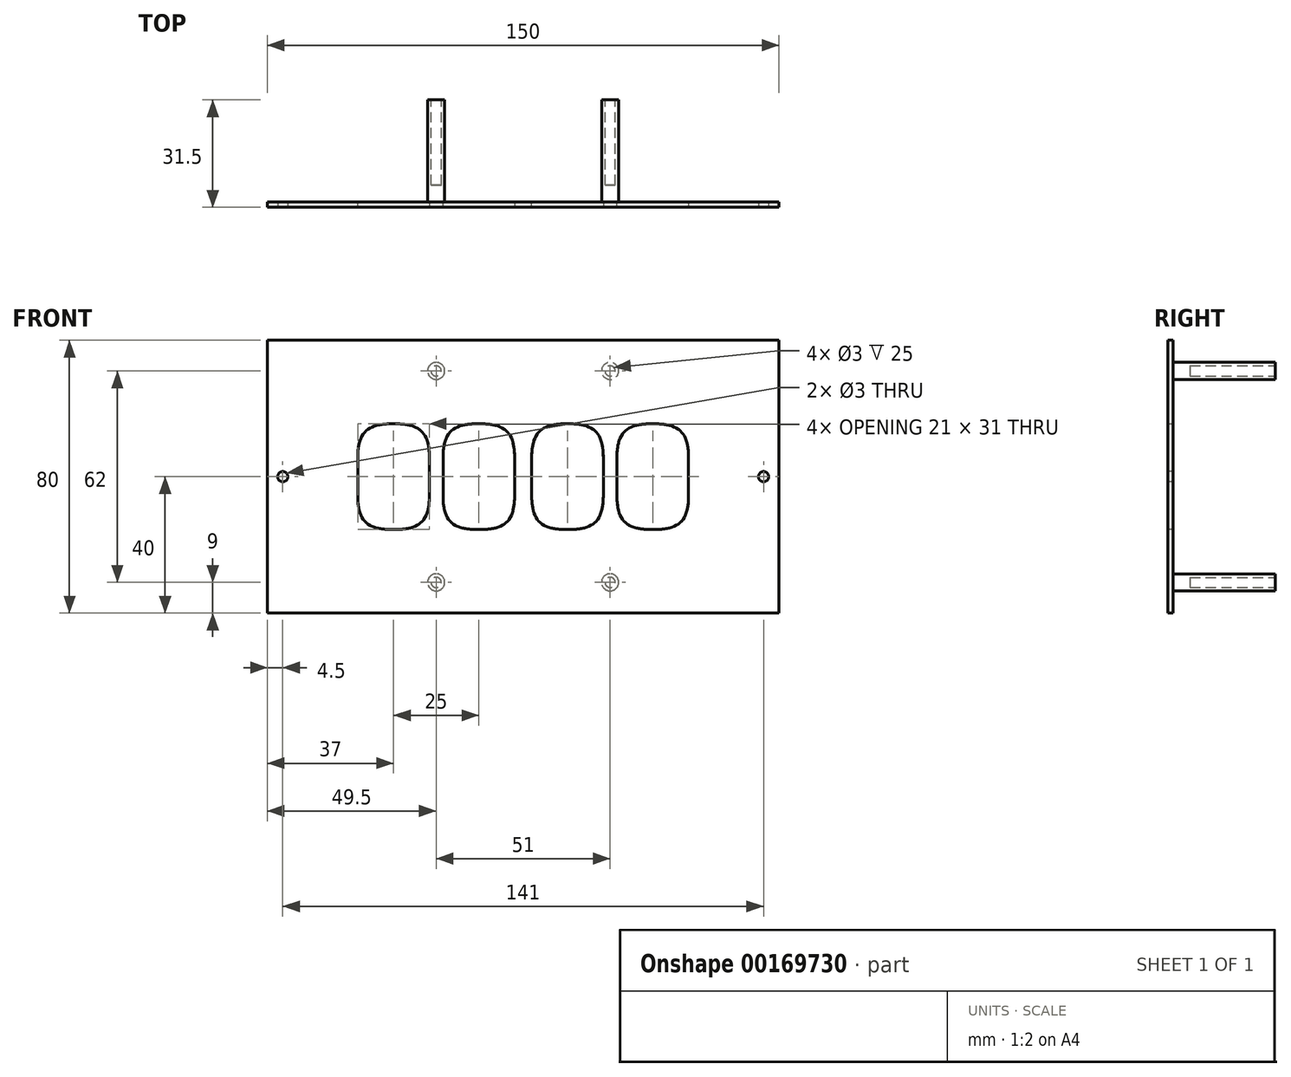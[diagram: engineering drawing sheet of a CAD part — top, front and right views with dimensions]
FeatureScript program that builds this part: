
annotation { "Feature Type Name" : "Feature", "Feature Type Description" : "" }
export const myFeature = defineFeature(function(context is Context, id is Id, definition is map)
    precondition{}
    {
        {
            var Q0;
            Q0=qCreatedBy(makeId("Front.planeOp"),FACE);
            var sketch = newSketch(context, id + "F0", { "sketchPlane" : qUnion([Q0])});
            skLineSegment(sketch, "E0.bottom", {"start": v(75, 40) * mm, "end": v(-75, 40) * mm});
            skLineSegment(sketch, "E0.top", {"start": v(75, -40) * mm, "end": v(-75, -40) * mm});
            skLineSegment(sketch, "E0.left", {"start": v(75, 40) * mm, "end": v(75, -40) * mm});
            skLineSegment(sketch, "E0.right", {"start": v(-75, 40) * mm, "end": v(-75, -40) * mm});
            skSolve(sketch);
        }
        {
            var Q0;
            Q0=makeQuery(id+"F0.imprint","IMPRINT",FACE,{"disambiguationData":[TD([[makeQuery(id+"F0.imprint","IMPRINT",EDGE,{"derivedFrom":sQuery(id+"F0.wireOp",EDGE,"E0.bottom")}),1.0]])]});
            extrude(context, id + "F1", {"entities" : qUnion([Q0]), "depth" : 1.5 * mm});
        }
        {
            var Q0;
            Q0=makeQuery(id+"F1.opExtrude","CAP_FACE",FACE,{"disambiguationData":[OSD([sQuery(id+"F0.wireOp",EDGE,"E0.bottom"),sQuery(id+"F0.wireOp",EDGE,"E0.top"),sQuery(id+"F0.wireOp",EDGE,"E0.left"),sQuery(id+"F0.wireOp",EDGE,"E0.right")])],"isStart":true});
            var sketch = newSketch(context, id + "F2", { "sketchPlane" : qUnion([Q0])});
            skCircle(sketch, "E1", {"center": v(-25.5, 31) * mm, "radius": 2.5 * mm});
            skCircle(sketch, "E2", {"center": v(-25.5, -31) * mm, "radius": 2.5 * mm});
            skCircle(sketch, "E3", {"center": v(25.5, -31) * mm, "radius": 2.5 * mm});
            skCircle(sketch, "E4", {"center": v(25.5, 31) * mm, "radius": 2.5 * mm});
            skSolve(sketch);
        }
        {
            var Q0;
            Q0 = qSketchRegion(id + "F2", true);
            extrude(context, id + "F3", {"entities" : qUnion([Q0]), "operationType" : NewBodyOperationType.ADD, "depth" : 30 * mm});
        }
        {
            var Q0;
            Q0=makeQuery(id+"F3.opExtrude","CAP_FACE",FACE,{"disambiguationData":[OSD([sQuery(id+"F2.wireOp",EDGE,"E1")])],"isStart":false});
            var sketch = newSketch(context, id + "F4", { "sketchPlane" : qUnion([Q0])});
            skCircle(sketch, "E5", {"center": v(-25.5, 31) * mm, "radius": 1.5 * mm});
            skSolve(sketch);
        }
        {
            var Q0;
            Q0=makeQuery(id+"F3.opExtrude","CAP_FACE",FACE,{"disambiguationData":[OSD([sQuery(id+"F2.wireOp",EDGE,"E4")])],"isStart":false});
            var sketch = newSketch(context, id + "F5", { "sketchPlane" : qUnion([Q0])});
            skCircle(sketch, "E6", {"center": v(25.5, 31) * mm, "radius": 1.5 * mm});
            skSolve(sketch);
        }
        {
            var Q0;
            Q0=makeQuery(id+"F3.opExtrude","CAP_FACE",FACE,{"disambiguationData":[OSD([sQuery(id+"F2.wireOp",EDGE,"E2")])],"isStart":false});
            var sketch = newSketch(context, id + "F6", { "sketchPlane" : qUnion([Q0])});
            skCircle(sketch, "E7", {"center": v(-25.5, -31) * mm, "radius": 1.5 * mm});
            skSolve(sketch);
        }
        {
            var Q0;
            Q0=makeQuery(id+"F3.opExtrude","CAP_FACE",FACE,{"disambiguationData":[OSD([sQuery(id+"F2.wireOp",EDGE,"E3")])],"isStart":false});
            var sketch = newSketch(context, id + "F7", { "sketchPlane" : qUnion([Q0])});
            skCircle(sketch, "E8", {"center": v(25.5, -31) * mm, "radius": 1.5 * mm});
            skSolve(sketch);
        }
        {
            var Q0;
            Q0 = qSketchRegion(id + "F4", true);
            var Q1;
            Q1 = qSketchRegion(id + "F5", true);
            var Q2;
            Q2 = qSketchRegion(id + "F6", true);
            var Q3;
            Q3 = qSketchRegion(id + "F7", true);
            extrude(context, id + "F8", {"entities" : qUnion([Q0, Q1, Q2, Q3]), "operationType" : NewBodyOperationType.REMOVE, "oppositeDirection" : true, "depth" : 25 * mm});
        }
        {
            var Q0;
            Q0=makeQuery(id+"F1.opExtrude","CAP_FACE",FACE,{"disambiguationData":[OSD([sQuery(id+"F0.wireOp",EDGE,"E0.bottom"),sQuery(id+"F0.wireOp",EDGE,"E0.top"),sQuery(id+"F0.wireOp",EDGE,"E0.left"),sQuery(id+"F0.wireOp",EDGE,"E0.right")])],"isStart":false});
            var sketch = newSketch(context, id + "F9", { "sketchPlane" : qUnion([Q0])});
            skCircle(sketch, "E9", {"center": v(-70.5, 0) * mm, "radius": 1.5 * mm});
            skLineSegment(sketch, "E10.bottom", {"start": v(-48.5, 15.5) * mm, "end": v(-27.5, 15.5) * mm});
            skLineSegment(sketch, "E10.top", {"start": v(-48.5, -15.5) * mm, "end": v(-27.5, -15.5) * mm});
            skLineSegment(sketch, "E10.left", {"start": v(-48.5, 15.5) * mm, "end": v(-48.5, -15.5) * mm});
            skLineSegment(sketch, "E10.right", {"start": v(-27.5, 15.5) * mm, "end": v(-27.5, -15.5) * mm});
            skLineSegment(sketch, "E11.bottom", {"start": v(-23.5, 15.5) * mm, "end": v(-2.5, 15.5) * mm});
            skLineSegment(sketch, "E11.top", {"start": v(-23.5, -15.5) * mm, "end": v(-2.5, -15.5) * mm});
            skLineSegment(sketch, "E11.left", {"start": v(-23.5, 15.5) * mm, "end": v(-23.5, -15.5) * mm});
            skLineSegment(sketch, "E11.right", {"start": v(-2.5, 15.5) * mm, "end": v(-2.5, -15.5) * mm});
            skSolve(sketch);
        }
        {
            var Q0;
            Q0 = qSketchRegion(id + "F9", true);
            extrude(context, id + "F10", {"entities" : qUnion([Q0]), "operationType" : NewBodyOperationType.REMOVE, "oppositeDirection" : true, "depth" : 3 * mm});
        }
        {
            var Q0;
            Q0=makeQuery(id+"F10.boolean.opBoolean","COPY",FACE,{"derivedFrom":makeQuery(id+"F10.opExtrude","SWEPT_FACE",FACE,{"disambiguationData":[OSD([sQuery(id+"F9.wireOp",EDGE,"E9")])]})});
            var Q1;
            Q1=makeQuery(id+"F10.boolean.opBoolean","COPY",FACE,{"derivedFrom":makeQuery(id+"F10.opExtrude","SWEPT_FACE",FACE,{"disambiguationData":[OSD([sQuery(id+"F9.wireOp",EDGE,"E10.left")])]})});
            var Q2;
            Q2=makeQuery(id+"F10.boolean.opBoolean","COPY",FACE,{"derivedFrom":makeQuery(id+"F10.opExtrude","SWEPT_FACE",FACE,{"disambiguationData":[OSD([sQuery(id+"F9.wireOp",EDGE,"E11.left")])]})});
            var Q3;
            Q3=makeQuery(id+"F10.boolean.opBoolean","COPY",FACE,{"derivedFrom":makeQuery(id+"F10.opExtrude","SWEPT_FACE",FACE,{"disambiguationData":[OSD([sQuery(id+"F9.wireOp",EDGE,"E10.bottom")])]})});
            var Q4;
            Q4=makeQuery(id+"F10.boolean.opBoolean","COPY",FACE,{"derivedFrom":makeQuery(id+"F10.opExtrude","SWEPT_FACE",FACE,{"disambiguationData":[OSD([sQuery(id+"F9.wireOp",EDGE,"E10.right")])]})});
            var Q5;
            Q5=makeQuery(id+"F10.boolean.opBoolean","COPY",FACE,{"derivedFrom":makeQuery(id+"F10.opExtrude","SWEPT_FACE",FACE,{"disambiguationData":[OSD([sQuery(id+"F9.wireOp",EDGE,"E11.bottom")])]})});
            var Q6;
            Q6=makeQuery(id+"F10.boolean.opBoolean","COPY",FACE,{"derivedFrom":makeQuery(id+"F10.opExtrude","SWEPT_FACE",FACE,{"disambiguationData":[OSD([sQuery(id+"F9.wireOp",EDGE,"E11.right")])]})});
            var Q7;
            Q7=makeQuery(id+"F10.boolean.opBoolean","COPY",FACE,{"derivedFrom":makeQuery(id+"F10.opExtrude","SWEPT_FACE",FACE,{"disambiguationData":[OSD([sQuery(id+"F9.wireOp",EDGE,"E11.top")])]})});
            var Q8;
            Q8=makeQuery(id+"F10.boolean.opBoolean","COPY",FACE,{"derivedFrom":makeQuery(id+"F10.opExtrude","SWEPT_FACE",FACE,{"disambiguationData":[OSD([sQuery(id+"F9.wireOp",EDGE,"E10.top")])]})});
            var Q9;
            Q9=qCreatedBy(makeId("Right.planeOp"),FACE);
            mirror(context, id + "F11", {"patternType" : MirrorType.FACE, "faces" : qUnion([Q0, Q1, Q2, Q3, Q4, Q5, Q6, Q7, Q8]), "mirrorPlane" : qUnion([Q9])});
        }
        {
            var Q0;
            Q0=makeQuery(id+"F10.boolean.opBoolean","COPY",EDGE,{"derivedFrom":makeQuery(id+"F10.opExtrude","SWEPT_EDGE",EDGE,{"disambiguationData":[OSD([sQuery(id+"F9.wireOp",EDGE,"E10.bottom"),sQuery(id+"F9.wireOp",EDGE,"E10.left")])]})});
            var Q1;
            Q1=makeQuery(id+"F10.boolean.opBoolean","COPY",EDGE,{"derivedFrom":makeQuery(id+"F10.opExtrude","SWEPT_EDGE",EDGE,{"disambiguationData":[OSD([sQuery(id+"F9.wireOp",EDGE,"E10.bottom"),sQuery(id+"F9.wireOp",EDGE,"E10.right")])]})});
            var Q2;
            Q2=makeQuery(id+"F10.boolean.opBoolean","COPY",EDGE,{"derivedFrom":makeQuery(id+"F10.opExtrude","SWEPT_EDGE",EDGE,{"disambiguationData":[OSD([sQuery(id+"F9.wireOp",EDGE,"E10.top"),sQuery(id+"F9.wireOp",EDGE,"E10.left")])]})});
            var Q3;
            Q3=makeQuery(id+"F10.boolean.opBoolean","COPY",EDGE,{"derivedFrom":makeQuery(id+"F10.opExtrude","SWEPT_EDGE",EDGE,{"disambiguationData":[OSD([sQuery(id+"F9.wireOp",EDGE,"E10.top"),sQuery(id+"F9.wireOp",EDGE,"E10.right")])]})});
            var Q4;
            Q4=makeQuery(id+"F10.boolean.opBoolean","COPY",EDGE,{"derivedFrom":makeQuery(id+"F10.opExtrude","SWEPT_EDGE",EDGE,{"disambiguationData":[OSD([sQuery(id+"F9.wireOp",EDGE,"E11.top"),sQuery(id+"F9.wireOp",EDGE,"E11.right")])]})});
            var Q5;
            Q5=makeQuery(id+"F10.boolean.opBoolean","COPY",EDGE,{"derivedFrom":makeQuery(id+"F10.opExtrude","SWEPT_EDGE",EDGE,{"disambiguationData":[OSD([sQuery(id+"F9.wireOp",EDGE,"E11.bottom"),sQuery(id+"F9.wireOp",EDGE,"E11.left")])]})});
            var Q6;
            Q6=makeQuery(id+"F10.boolean.opBoolean","COPY",EDGE,{"derivedFrom":makeQuery(id+"F10.opExtrude","SWEPT_EDGE",EDGE,{"disambiguationData":[OSD([sQuery(id+"F9.wireOp",EDGE,"E11.top"),sQuery(id+"F9.wireOp",EDGE,"E11.left")])]})});
            var Q7;
            Q7=makeQuery(id+"F10.boolean.opBoolean","COPY",EDGE,{"derivedFrom":makeQuery(id+"F10.opExtrude","SWEPT_EDGE",EDGE,{"disambiguationData":[OSD([sQuery(id+"F9.wireOp",EDGE,"E11.bottom"),sQuery(id+"F9.wireOp",EDGE,"E11.right")])]})});
            var Q8;
            Q8=makeQuery(id+"F11.opPattern","COPY",EDGE,{"derivedFrom":makeQuery(id+"F10.boolean.opBoolean","COPY",EDGE,{"derivedFrom":makeQuery(id+"F10.opExtrude","SWEPT_EDGE",EDGE,{"disambiguationData":[OSD([sQuery(id+"F9.wireOp",EDGE,"E11.bottom"),sQuery(id+"F9.wireOp",EDGE,"E11.left")])]})}),"instanceName":"1"});
            var Q9;
            Q9=makeQuery(id+"F11.opPattern","COPY",EDGE,{"derivedFrom":makeQuery(id+"F10.boolean.opBoolean","COPY",EDGE,{"derivedFrom":makeQuery(id+"F10.opExtrude","SWEPT_EDGE",EDGE,{"disambiguationData":[OSD([sQuery(id+"F9.wireOp",EDGE,"E10.bottom"),sQuery(id+"F9.wireOp",EDGE,"E10.left")])]})}),"instanceName":"1"});
            var Q10;
            Q10=makeQuery(id+"F11.opPattern","COPY",EDGE,{"derivedFrom":makeQuery(id+"F10.boolean.opBoolean","COPY",EDGE,{"derivedFrom":makeQuery(id+"F10.opExtrude","SWEPT_EDGE",EDGE,{"disambiguationData":[OSD([sQuery(id+"F9.wireOp",EDGE,"E11.top"),sQuery(id+"F9.wireOp",EDGE,"E11.right")])]})}),"instanceName":"1"});
            var Q11;
            Q11=makeQuery(id+"F11.opPattern","COPY",EDGE,{"derivedFrom":makeQuery(id+"F10.boolean.opBoolean","COPY",EDGE,{"derivedFrom":makeQuery(id+"F10.opExtrude","SWEPT_EDGE",EDGE,{"disambiguationData":[OSD([sQuery(id+"F9.wireOp",EDGE,"E10.top"),sQuery(id+"F9.wireOp",EDGE,"E10.right")])]})}),"instanceName":"1"});
            var Q12;
            Q12=makeQuery(id+"F11.opPattern","COPY",EDGE,{"derivedFrom":makeQuery(id+"F10.boolean.opBoolean","COPY",EDGE,{"derivedFrom":makeQuery(id+"F10.opExtrude","SWEPT_EDGE",EDGE,{"disambiguationData":[OSD([sQuery(id+"F9.wireOp",EDGE,"E10.bottom"),sQuery(id+"F9.wireOp",EDGE,"E10.right")])]})}),"instanceName":"1"});
            var Q13;
            Q13=makeQuery(id+"F11.opPattern","COPY",EDGE,{"derivedFrom":makeQuery(id+"F10.boolean.opBoolean","COPY",EDGE,{"derivedFrom":makeQuery(id+"F10.opExtrude","SWEPT_EDGE",EDGE,{"disambiguationData":[OSD([sQuery(id+"F9.wireOp",EDGE,"E11.bottom"),sQuery(id+"F9.wireOp",EDGE,"E11.right")])]})}),"instanceName":"1"});
            var Q14;
            Q14=makeQuery(id+"F11.opPattern","COPY",EDGE,{"derivedFrom":makeQuery(id+"F10.boolean.opBoolean","COPY",EDGE,{"derivedFrom":makeQuery(id+"F10.opExtrude","SWEPT_EDGE",EDGE,{"disambiguationData":[OSD([sQuery(id+"F9.wireOp",EDGE,"E10.top"),sQuery(id+"F9.wireOp",EDGE,"E10.left")])]})}),"instanceName":"1"});
            var Q15;
            Q15=makeQuery(id+"F11.opPattern","COPY",EDGE,{"derivedFrom":makeQuery(id+"F10.boolean.opBoolean","COPY",EDGE,{"derivedFrom":makeQuery(id+"F10.opExtrude","SWEPT_EDGE",EDGE,{"disambiguationData":[OSD([sQuery(id+"F9.wireOp",EDGE,"E11.top"),sQuery(id+"F9.wireOp",EDGE,"E11.left")])]})}),"instanceName":"1"});
            fillet(context, id + "F12", {"entities" : qUnion([Q0, Q1, Q2, Q3, Q4, Q5, Q6, Q7, Q8, Q9, Q10, Q11, Q12, Q13, Q14, Q15]), "radius" : 10 * mm, "tangentPropagation" : true, "rho" : 0.55, "crossSection" : FilletCrossSection.CONIC, "allowEdgeOverflow" : false});
        }
    });
